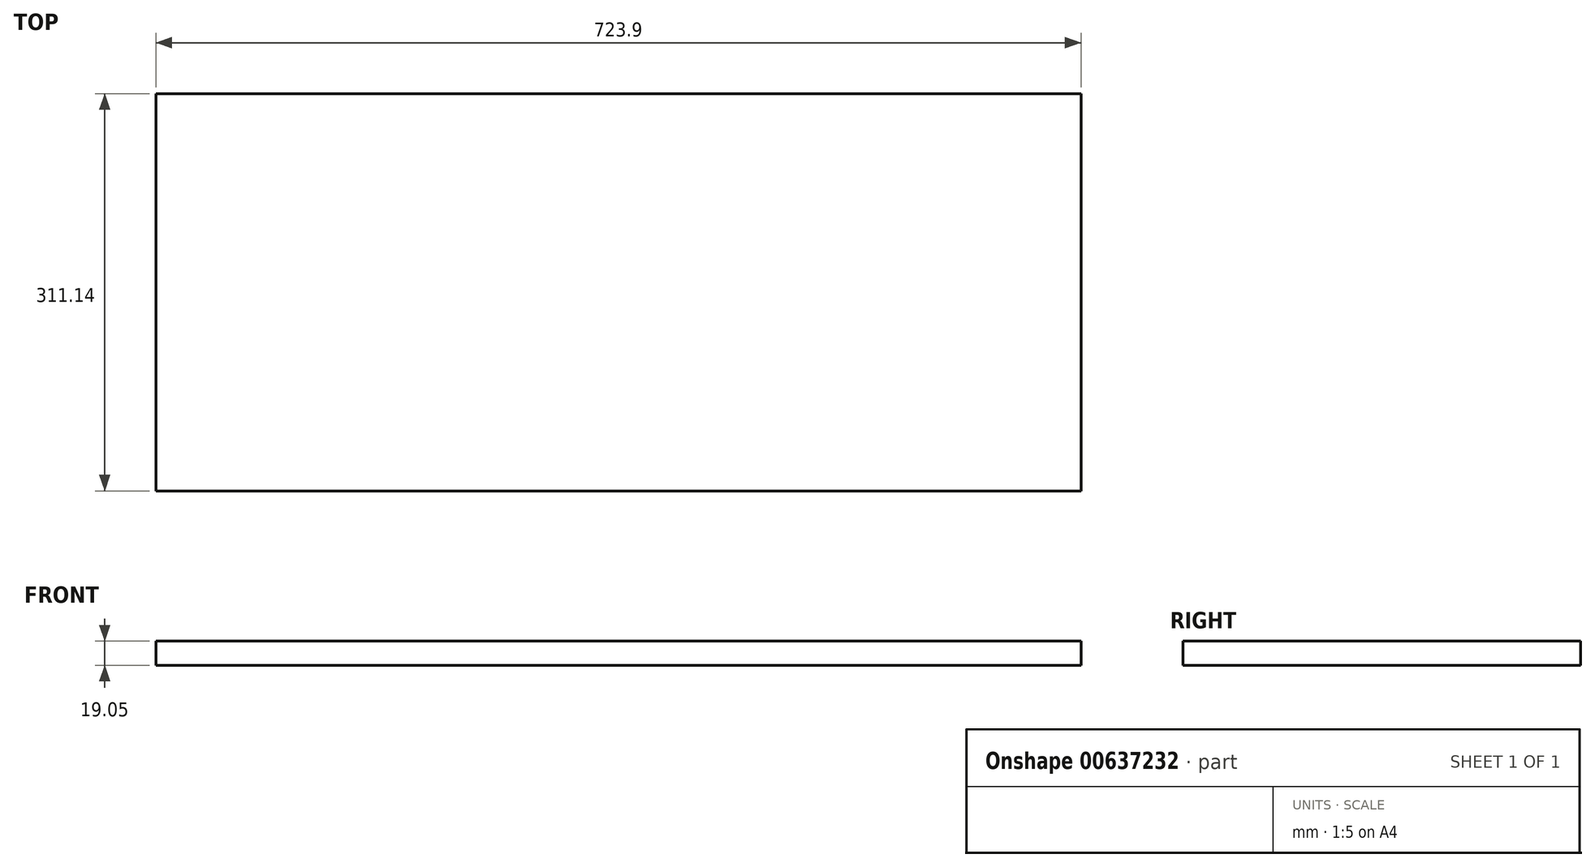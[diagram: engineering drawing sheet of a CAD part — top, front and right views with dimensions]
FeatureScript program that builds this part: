
annotation { "Feature Type Name" : "Feature", "Feature Type Description" : "" }
export const myFeature = defineFeature(function(context is Context, id is Id, definition is map)
    precondition{}
    {
        {
            var Q0;
            Q0=qCreatedBy(makeId("Top.planeOp"),FACE);
            var sketch = newSketch(context, id + "F0", { "sketchPlane" : qUnion([Q0])});
            skLineSegment(sketch, "E0.bottom", {"start": v(-361.95, 155.58) * mm, "end": v(361.95, 155.58) * mm});
            skLineSegment(sketch, "E0.top", {"start": v(-361.95, -155.57) * mm, "end": v(361.95, -155.57) * mm});
            skLineSegment(sketch, "E0.left", {"start": v(-361.95, 155.58) * mm, "end": v(-361.95, -155.57) * mm});
            skLineSegment(sketch, "E0.right", {"start": v(361.95, 155.58) * mm, "end": v(361.95, -155.57) * mm});
            skPoint(sketch, "E0.middle", {"position": v(0, 0) * mm});
            skSolve(sketch);
        }
        {
            var Q0;
            Q0=makeQuery(id+"F0.imprint","IMPRINT",FACE,{"disambiguationData":[TD([[makeQuery(id+"F0.imprint","IMPRINT",EDGE,{"derivedFrom":sQuery(id+"F0.wireOp",EDGE,"E0.bottom")}),-1.0]])]});
            extrude(context, id + "F1", {"entities" : qUnion([Q0]), "depth" : 19.05 * mm, "offsetDistance" : 25.4 * mm});
        }
    });
